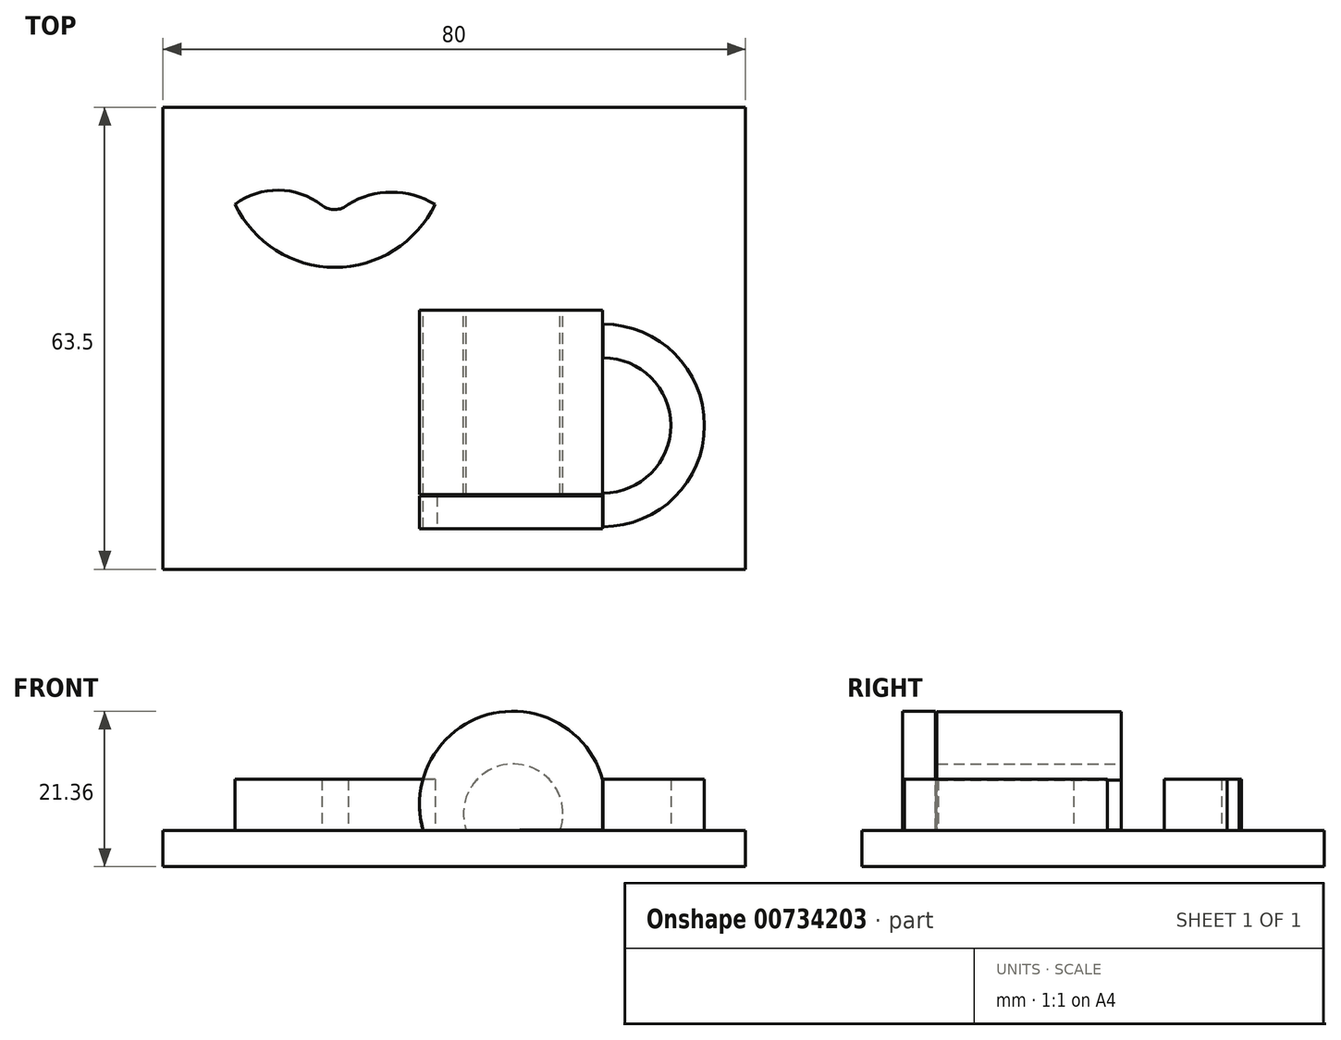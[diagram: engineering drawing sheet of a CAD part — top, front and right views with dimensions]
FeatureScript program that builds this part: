
annotation { "Feature Type Name" : "Feature", "Feature Type Description" : "" }
export const myFeature = defineFeature(function(context is Context, id is Id, definition is map)
    precondition{}
    {
        {
            var Q0;
            Q0=qCreatedBy(makeId("Top.planeOp"),FACE);
            var sketch = newSketch(context, id + "F0", { "sketchPlane" : qUnion([Q0])});
            skLineSegment(sketch, "E0.bottom", {"start": v(40, -33.5) * mm, "end": v(-40, -33.5) * mm});
            skLineSegment(sketch, "E0.top", {"start": v(40, 30) * mm, "end": v(-40, 30) * mm});
            skLineSegment(sketch, "E0.left", {"start": v(40, -30) * mm, "end": v(40, 30) * mm});
            skLineSegment(sketch, "E0.right", {"start": v(-40, -30) * mm, "end": v(-40, 30) * mm});
            skPoint(sketch, "E0.middle", {"position": v(0, 0) * mm});
            skLineSegment(sketch, "E1", {"start": v(-40, -32.5) * mm, "end": v(-40, -30) * mm});
            skLineSegment(sketch, "E2", {"start": v(40, -32.5) * mm, "end": v(40, -30) * mm});
            skLineSegment(sketch, "E3", {"start": v(-40, -33.5) * mm, "end": v(-40, -32.5) * mm});
            skLineSegment(sketch, "E4", {"start": v(40, -33.5) * mm, "end": v(40, -32.5) * mm});
            skSolve(sketch);
        }
        {
            var Q0;
            Q0=qCreatedBy(makeId("Top.planeOp"),FACE);
            var sketch = newSketch(context, id + "F1", { "sketchPlane" : qUnion([Q0])});
            skLineSegment(sketch, "E5.bottom", {"start": v(37, 29.06) * mm, "end": v(-37, 29.06) * mm});
            skLineSegment(sketch, "E5.top", {"start": v(37, -33.44) * mm, "end": v(-37, -33.44) * mm});
            skLineSegment(sketch, "E5.left", {"start": v(39.5, 29.06) * mm, "end": v(39.5, -30.94) * mm});
            skLineSegment(sketch, "E5.right", {"start": v(-39.5, 29.06) * mm, "end": v(-39.5, -30.94) * mm});
            skLineSegment(sketch, "E6", {"start": v(-39.5, 29.06) * mm, "end": v(-37, 29.06) * mm});
            skLineSegment(sketch, "E7", {"start": v(37, 29.06) * mm, "end": v(39.5, 29.06) * mm});
            skLineSegment(sketch, "E8", {"start": v(39.5, -30.94) * mm, "end": v(39.5, -33.44) * mm});
            skLineSegment(sketch, "E9", {"start": v(39.5, -33.44) * mm, "end": v(37, -33.44) * mm});
            skLineSegment(sketch, "E10", {"start": v(-39.5, -30.94) * mm, "end": v(-39.5, -33.44) * mm});
            skLineSegment(sketch, "E11", {"start": v(-39.5, -33.44) * mm, "end": v(-37, -33.44) * mm});
            skArc(sketch, "E12", {"start": v(-18.18, 16.54) * mm, "mid": v(-24.12, 18.6) * mm, "end": v(-30.1, 16.67) * mm});
            skArc(sketch, "E13", {"start": v(-18.18, 16.54) * mm, "mid": v(-16.36, 15.93) * mm, "end": v(-14.58, 16.67) * mm});
            skArc(sketch, "E14", {"start": v(-2.65, 16.67) * mm, "mid": v(-8.62, 18.31) * mm, "end": v(-14.58, 16.67) * mm});
            skArc(sketch, "E15", {"start": v(-30.1, 16.67) * mm, "mid": v(-16.38, 12.46) * mm, "end": v(-2.65, 16.67) * mm});
            skArc(sketch, "E16", {"start": v(-30.1, 16.67) * mm, "mid": v(-16.38, 8) * mm, "end": v(-2.65, 16.67) * mm});
            skArc(sketch, "E17", {"start": v(20.44, -27.64) * mm, "mid": v(34.36, -13.73) * mm, "end": v(20.44, 0.2) * mm});
            skArc(sketch, "E18", {"start": v(20.44, -23.03) * mm, "mid": v(29.74, -13.73) * mm, "end": v(20.44, -4.43) * mm});
            skLineSegment(sketch, "E19", {"start": v(20.44, 0.2) * mm, "end": v(20.44, -4.43) * mm});
            skLineSegment(sketch, "E20.trimOffspring", {"start": v(20.44, -23.03) * mm, "end": v(20.44, -27.64) * mm});
            skSolve(sketch);
        }
        {
            var Q0;
            Q0 = qSketchRegion(id + "F0", true);
            extrude(context, id + "F2", {"entities" : qUnion([Q0]), "depth" : 5 * mm, "offsetDistance" : 25 * mm});
        }
        {
            var Q0;
            Q0=makeQuery(id+"F1.imprint","IMPRINT",FACE,{"disambiguationData":[TD([[makeQuery(id+"F1.imprint","IMPRINT",EDGE,{"derivedFrom":sQuery(id+"F1.wireOp",EDGE,"E15")}),-1.0]])]});
            var Q1;
            Q1=makeQuery(id+"F1.imprint","IMPRINT",FACE,{"disambiguationData":[TD([[makeQuery(id+"F1.imprint","IMPRINT",EDGE,{"derivedFrom":sQuery(id+"F1.wireOp",EDGE,"E12")}),1.0]])]});
            var Q2;
            Q2=makeQuery(id+"F1.imprint","IMPRINT",FACE,{"disambiguationData":[TD([[makeQuery(id+"F1.imprint","IMPRINT",EDGE,{"derivedFrom":sQuery(id+"F1.wireOp",EDGE,"E17")}),1.0]])]});
            extrude(context, id + "F3", {"entities" : qUnion([Q0, Q1, Q2]), "operationType" : NewBodyOperationType.ADD, "depth" : 12 * mm, "offsetDistance" : 25 * mm});
        }
        {
            var Q0;
            Q0=qCreatedBy(makeId("Front.planeOp"),FACE);
            var sketch = newSketch(context, id + "F4", { "sketchPlane" : qUnion([Q0])});
            skArc(sketch, "E21", {"start": v(20.4, 11.92) * mm, "mid": v(4.55, 20.82) * mm, "end": v(-4.27, 4.93) * mm});
            skArc(sketch, "E22", {"start": v(14.52, 4.97) * mm, "mid": v(8.32, 14.1) * mm, "end": v(1.52, 5.41) * mm});
            skLineSegment(sketch, "E23", {"start": v(20.4, 5.05) * mm, "end": v(20.4, 11.92) * mm});
            skLineSegment(sketch, "E24", {"start": v(-4.27, 4.93) * mm, "end": v(1.64, 4.96) * mm});
            skLineSegment(sketch, "E25", {"start": v(1.52, 5.41) * mm, "end": v(1.64, 4.96) * mm});
            skLineSegment(sketch, "E26.trimOffspring", {"start": v(14.54, 5.02) * mm, "end": v(20.4, 5.05) * mm});
            skSolve(sketch);
        }
        {
            var Q0;
            Q0=qCreatedBy(makeId("Front.planeOp"),FACE);
            var sketch = newSketch(context, id + "F5", { "sketchPlane" : qUnion([Q0])});
            skArc(sketch, "E27", {"start": v(20.4, 11.98) * mm, "mid": v(4.55, 20.88) * mm, "end": v(-4.27, 5) * mm});
            skArc(sketch, "E28", {"start": v(14.52, 5.03) * mm, "mid": v(14.53, 5.05) * mm, "end": v(14.54, 5.08) * mm});
            skLineSegment(sketch, "E29", {"start": v(20.4, 5.1) * mm, "end": v(20.4, 11.98) * mm});
            skLineSegment(sketch, "E30", {"start": v(-4.27, 5) * mm, "end": v(20.4, 5.1) * mm});
            skSolve(sketch);
        }
        {
            var Q0;
            Q0 = qSketchRegion(id + "F5", true);
            extrude(context, id + "F6", {"entities" : qUnion([Q0]), "operationType" : NewBodyOperationType.ADD, "depth" : 27.9 * mm, "offsetDistance" : 25 * mm, "hasSecondDirection" : true, "secondDirectionOppositeDirection" : false, "secondDirectionDepth" : 23.4 * mm});
        }
        {
            var Q0;
            Q0 = qSketchRegion(id + "F4", true);
            extrude(context, id + "F7", {"entities" : qUnion([Q0]), "operationType" : NewBodyOperationType.ADD, "depth" : 23.2 * mm, "offsetDistance" : 25 * mm, "hasSecondDirection" : true, "secondDirectionOppositeDirection" : true, "secondDirectionDepth" : 2.1 * mm});
        }
    });
